# Revit family: Saxi Teanik 500 Nät
name_source: partatom
category: Mechanical Equipment
revit_build: Autodesk Revit Architecture 2015 (Build: 20140322_1515(x64)
units: mm (PartAtom-declared; Revit-internal decimal feet)

## types (1)
- Saxi Teanik 500 Nät
    Bracket_Height_OMV = 7650 mm  [stored 25.0984 ft]
    Bracket_Offset = 3000 mm  [stored 9.84252 ft]
    Brackets_Array_Visible = Yes
    Brackets_Single_Visible = No
    First_Bracket = 10000 mm  [stored 32.8084 ft]
    First_Bracket_From_Edge = 250 mm  [stored 0.82021 ft]
    Last_Bracket = 22750 mm  [stored 74.6391 ft]
    Machinery_Height = 7750 mm  [stored 25.4265 ft]
    Manufacturer = Saxi Vägg AB
    Model = Saxi Teanik 500 Nät
    Motor_Height_OMV = 7833 mm  [stored 25.6988 ft]
    Motor_Placement = 11425 mm  [stored 37.4836 ft]
    NO_Brackets = 3
    NO_brackets_REAL = 3
    Net_Height = 4150 mm  [stored 13.6155 ft]
    Shaft_Legth = 22850 mm  [stored 74.9672 ft]
    Tissue_Height = 7000 mm  [stored 22.9659 ft]
    To_Shaft = 7795 mm  [stored 25.5741 ft]
    UK_Upphissad = 7000 mm  [stored 22.9659 ft]
    URL = http://www.saxi.se
    Width = 23000 mm  [stored 75.4593 ft]

note: [stored X ft] marks values corroborated as IEEE doubles in the binary element streams (Revit-internal decimal feet)

## geometry (parser evidence)
native form markers: Sweep x9
no freeform markers — native parametric forms only
